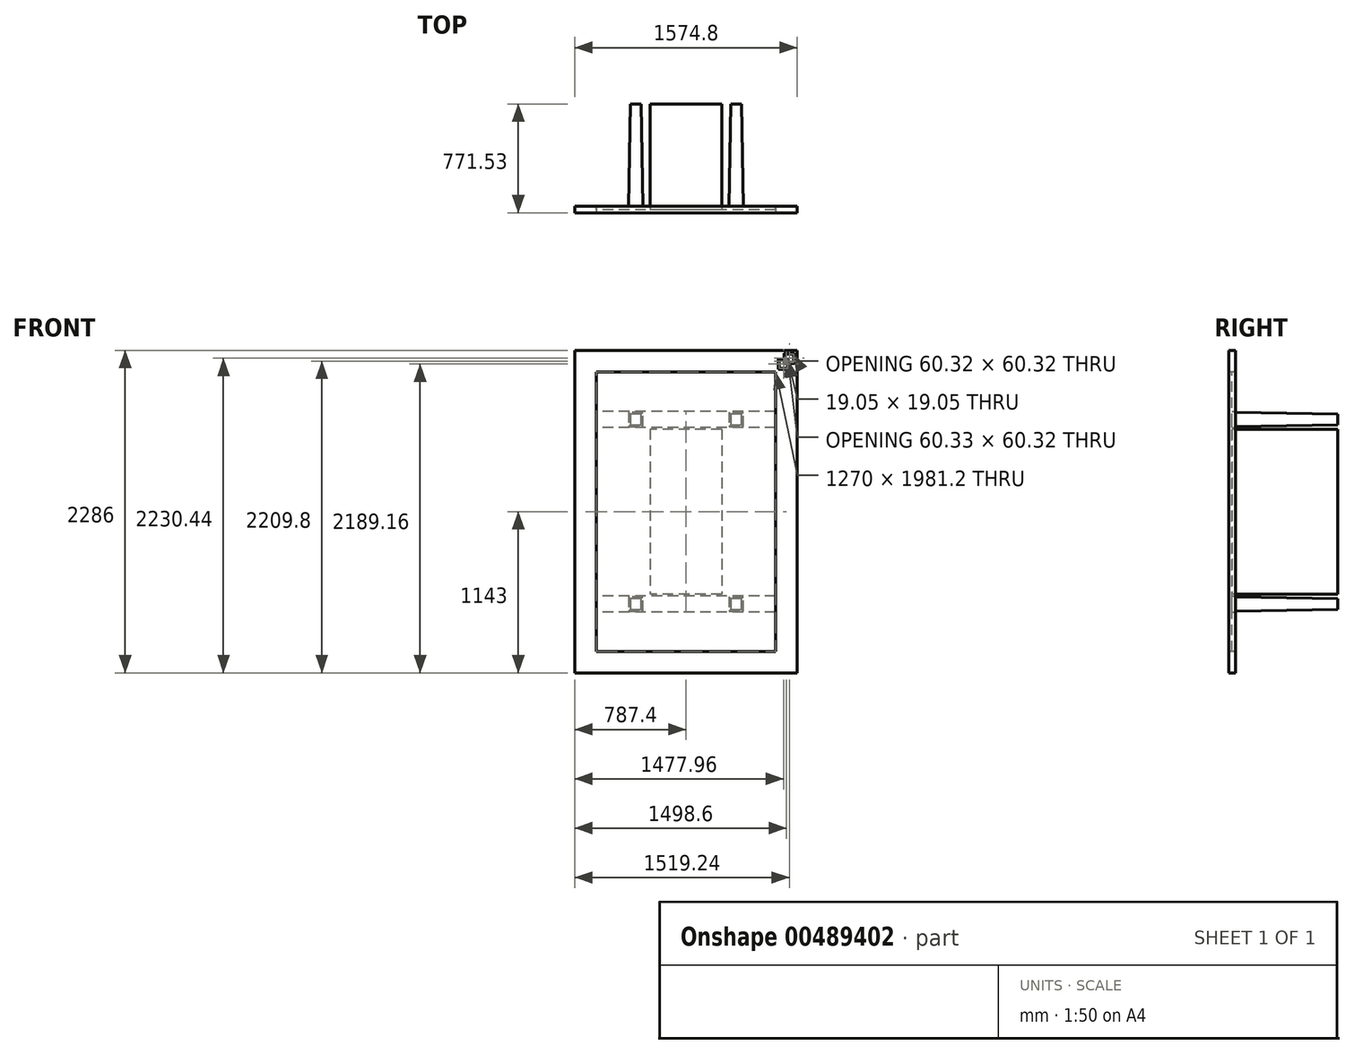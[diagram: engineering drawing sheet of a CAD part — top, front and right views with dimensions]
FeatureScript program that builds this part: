
annotation { "Feature Type Name" : "Feature", "Feature Type Description" : "" }
export const myFeature = defineFeature(function(context is Context, id is Id, definition is map)
    precondition{}
    {
        {
            var Q0;
            Q0=qCreatedBy(makeId("Front.planeOp"),FACE);
            var sketch = newSketch(context, id + "F0", { "sketchPlane" : qUnion([Q0])});
            skLineSegment(sketch, "E0.bottom", {"start": v(0, 0) * mm, "end": v(-1574.8, 0) * mm});
            skLineSegment(sketch, "E0.top", {"start": v(0, 2286) * mm, "end": v(-1574.8, 2286) * mm});
            skLineSegment(sketch, "E0.left", {"start": v(0, 0) * mm, "end": v(0, 2286) * mm});
            skLineSegment(sketch, "E0.right", {"start": v(-1574.8, 0) * mm, "end": v(-1574.8, 2286) * mm});
            skLineSegment(sketch, "E1.0", {"start": v(-152.4, 2133.6) * mm, "end": v(-1422.4, 2133.6) * mm});
            skLineSegment(sketch, "E1.1", {"start": v(-152.4, 152.4) * mm, "end": v(-152.4, 2133.6) * mm});
            skLineSegment(sketch, "E1.2", {"start": v(-152.4, 152.4) * mm, "end": v(-1422.4, 152.4) * mm});
            skLineSegment(sketch, "E1.3", {"start": v(-1422.4, 152.4) * mm, "end": v(-1422.4, 2133.6) * mm});
            skLineSegment(sketch, "E2", {"start": v(-1422.4, 2133.6) * mm, "end": v(-1574.8, 2133.6) * mm});
            skLineSegment(sketch, "E3", {"start": v(-152.4, 2133.6) * mm, "end": v(0, 2133.6) * mm});
            skLineSegment(sketch, "E4", {"start": v(-152.4, 152.4) * mm, "end": v(0, 152.4) * mm});
            skLineSegment(sketch, "E5", {"start": v(-1422.4, 152.4) * mm, "end": v(-1574.8, 152.4) * mm});
            skSolve(sketch);
        }
        {
            var Q0;
            {var subQ1=sQuery(id+"F0.wireOp",EDGE,"E0.top");Q0=makeQuery(id+"F0.imprint","IMPRINT",FACE,{"disambiguationData":[TD([[makeQuery(id+"F0.imprint","IMPRINT",EDGE,{"derivedFrom":subQ1}),1.0]])]});}
            var Q1;
            Q1=makeQuery(id+"F0.imprint","IMPRINT",FACE,{"disambiguationData":[TD([[makeQuery(id+"F0.imprint","IMPRINT",EDGE,{"derivedFrom":sQuery(id+"F0.wireOp",EDGE,"E1.3")}),1.0]])]});
            var Q2;
            Q2=makeQuery(id+"F0.imprint","IMPRINT",FACE,{"disambiguationData":[TD([[makeQuery(id+"F0.imprint","IMPRINT",EDGE,{"derivedFrom":sQuery(id+"F0.wireOp",EDGE,"E1.1")}),-1.0]])]});
            var Q3;
            {var subQ1=sQuery(id+"F0.wireOp",EDGE,"E0.bottom");Q3=makeQuery(id+"F0.imprint","IMPRINT",FACE,{"disambiguationData":[TD([[makeQuery(id+"F0.imprint","IMPRINT",EDGE,{"derivedFrom":subQ1}),-1.0]])]});}
            extrude(context, id + "F1", {"entities" : qUnion([Q0, Q1, Q2, Q3]), "oppositeDirection" : true, "depth" : 47.62 * mm, "offsetDistance" : 25.4 * mm});
        }
        {
            var Q0;
            Q0=makeQuery(id+"F0.imprint","IMPRINT",FACE,{"disambiguationData":[TD([[makeQuery(id+"F0.imprint","IMPRINT",EDGE,{"derivedFrom":sQuery(id+"F0.wireOp",EDGE,"E1.0")}),1.0]])]});
            extrude(context, id + "F2", {"entities" : qUnion([Q0]), "oppositeDirection" : true, "depth" : 22.22 * mm, "offsetDistance" : 25.4 * mm});
        }
        {
            var Q0;
            Q0=makeQuery(id+"F1.opExtrude","SWEPT_FACE",FACE,{"disambiguationData":[OSD([sQuery(id+"F0.wireOp",EDGE,"E1.3")])]});
            var sketch = newSketch(context, id + "F3", { "sketchPlane" : qUnion([Q0])});
            skLineSegment(sketch, "E6.bottom", {"start": v(22.23, 431.8) * mm, "end": v(47.62, 431.8) * mm});
            skLineSegment(sketch, "E6.top", {"start": v(22.22, 546.1) * mm, "end": v(47.63, 546.1) * mm});
            skLineSegment(sketch, "E6.left", {"start": v(22.23, 431.8) * mm, "end": v(22.22, 546.1) * mm});
            skLineSegment(sketch, "E6.right", {"start": v(47.63, 431.8) * mm, "end": v(47.63, 546.1) * mm});
            skLineSegment(sketch, "E7.bottom", {"start": v(22.23, 1739.9) * mm, "end": v(47.63, 1739.9) * mm});
            skLineSegment(sketch, "E7.top", {"start": v(22.23, 1854.2) * mm, "end": v(47.63, 1854.2) * mm});
            skLineSegment(sketch, "E7.left", {"start": v(22.23, 1739.9) * mm, "end": v(22.23, 1854.2) * mm});
            skLineSegment(sketch, "E7.right", {"start": v(47.63, 1739.9) * mm, "end": v(47.63, 1854.2) * mm});
            skSolve(sketch);
        }
        {
            var Q0;
            Q0=makeQuery(id+"F3.imprint","IMPRINT",FACE,{"disambiguationData":[TD([[makeQuery(id+"F3.imprint","IMPRINT",EDGE,{"derivedFrom":sQuery(id+"F3.wireOp",EDGE,"E6.bottom")}),1.0]])]});
            var Q1;
            Q1=makeQuery(id+"F3.imprint","IMPRINT",FACE,{"disambiguationData":[TD([[makeQuery(id+"F3.imprint","IMPRINT",EDGE,{"derivedFrom":sQuery(id+"F3.wireOp",EDGE,"E7.bottom")}),1.0]])]});
            var Q2;
            Q2=makeQuery(id+"F1.opExtrude","SWEPT_FACE",FACE,{"disambiguationData":[OSD([sQuery(id+"F0.wireOp",EDGE,"E1.1")])]});
            extrude(context, id + "F4", {"entities" : qUnion([Q0, Q1]), "endBound" : BoundingType.UP_TO_SURFACE, "depth" : 25.4 * mm, "endBoundEntityFace" : qUnion([Q2]), "offsetDistance" : 25.4 * mm});
        }
        {
            var Q0;
            Q0=makeQuery(id+"F1.opExtrude","CAP_FACE",FACE,{"disambiguationData":[OSD([sQuery(id+"F0.wireOp",EDGE,"E0.bottom"),sQuery(id+"F0.wireOp",EDGE,"E0.top"),sQuery(id+"F0.wireOp",EDGE,"E0.left"),sQuery(id+"F0.wireOp",EDGE,"E0.right"),sQuery(id+"F0.wireOp",EDGE,"E1.0"),sQuery(id+"F0.wireOp",EDGE,"E1.1"),sQuery(id+"F0.wireOp",EDGE,"E1.2"),sQuery(id+"F0.wireOp",EDGE,"E1.3")])],"isStart":false});
            var sketch = newSketch(context, id + "F5", { "sketchPlane" : qUnion([Q0])});
            skLineSegment(sketch, "E8.bottom", {"start": v(381, 1847.53) * mm, "end": v(482.6, 1847.53) * mm});
            skLineSegment(sketch, "E8.top", {"start": v(381, 1745.93) * mm, "end": v(482.6, 1745.93) * mm});
            skLineSegment(sketch, "E8.left", {"start": v(381, 1847.53) * mm, "end": v(381, 1745.93) * mm});
            skLineSegment(sketch, "E8.right", {"start": v(482.6, 1847.53) * mm, "end": v(482.6, 1745.93) * mm});
            skLineSegment(sketch, "E9.0.1.0", {"start": v(482.6, 539.43) * mm, "end": v(482.6, 437.83) * mm});
            skLineSegment(sketch, "E9.0.1.1", {"start": v(381, 539.43) * mm, "end": v(381, 437.83) * mm});
            skLineSegment(sketch, "E9.0.1.2", {"start": v(381, 437.83) * mm, "end": v(482.6, 437.83) * mm});
            skLineSegment(sketch, "E9.0.1.3", {"start": v(381, 539.43) * mm, "end": v(482.6, 539.43) * mm});
            skLineSegment(sketch, "E9.1.0.0", {"start": v(1193.8, 1847.53) * mm, "end": v(1193.8, 1745.93) * mm});
            skLineSegment(sketch, "E9.1.0.1", {"start": v(1092.2, 1847.53) * mm, "end": v(1092.2, 1745.93) * mm});
            skLineSegment(sketch, "E9.1.0.2", {"start": v(1092.2, 1745.93) * mm, "end": v(1193.8, 1745.93) * mm});
            skLineSegment(sketch, "E9.1.0.3", {"start": v(1092.2, 1847.53) * mm, "end": v(1193.8, 1847.53) * mm});
            skLineSegment(sketch, "E9.1.1.0", {"start": v(1193.8, 539.43) * mm, "end": v(1193.8, 437.83) * mm});
            skLineSegment(sketch, "E9.1.1.1", {"start": v(1092.2, 539.43) * mm, "end": v(1092.2, 437.83) * mm});
            skLineSegment(sketch, "E9.1.1.2", {"start": v(1092.2, 437.83) * mm, "end": v(1193.8, 437.83) * mm});
            skLineSegment(sketch, "E9.1.1.3", {"start": v(1092.2, 539.43) * mm, "end": v(1193.8, 539.43) * mm});
            skLineSegment(sketch, "E9.direction1", {"start": v(381, 1745.93) * mm, "end": v(1092.2, 1745.93) * mm, "construction": true});
            skLineSegment(sketch, "E9.direction2", {"start": v(381, 1745.93) * mm, "end": v(381, 437.83) * mm, "construction": true});
            skSolve(sketch);
        }
        {
            var Q0;
            Q0=makeQuery(id+"F5.imprint","IMPRINT",FACE,{"disambiguationData":[TD([[makeQuery(id+"F5.imprint","IMPRINT",EDGE,{"derivedFrom":sQuery(id+"F5.wireOp",EDGE,"E8.bottom")}),-1.0]])]});
            var Q1;
            Q1=makeQuery(id+"F5.imprint","IMPRINT",FACE,{"disambiguationData":[TD([[makeQuery(id+"F5.imprint","IMPRINT",EDGE,{"derivedFrom":sQuery(id+"F5.wireOp",EDGE,"E9.1.0.0")}),-1.0]])]});
            var Q2;
            Q2=makeQuery(id+"F5.imprint","IMPRINT",FACE,{"disambiguationData":[TD([[makeQuery(id+"F5.imprint","IMPRINT",EDGE,{"derivedFrom":sQuery(id+"F5.wireOp",EDGE,"E9.0.1.0")}),-1.0]])]});
            var Q3;
            Q3=makeQuery(id+"F5.imprint","IMPRINT",FACE,{"disambiguationData":[TD([[makeQuery(id+"F5.imprint","IMPRINT",EDGE,{"derivedFrom":sQuery(id+"F5.wireOp",EDGE,"E9.1.1.0")}),-1.0]])]});
            extrude(context, id + "F6", {"entities" : qUnion([Q0, Q1, Q2, Q3]), "depth" : 723.9 * mm, "offsetDistance" : 25.4 * mm, "hasDraft" : true, "draftAngle" : 1 * degree, "draftPullDirection" : true});
        }
        {
            var Q0;
            Q0=makeQuery(id+"F2.opExtrude","CAP_FACE",FACE,{"disambiguationData":[OSD([sQuery(id+"F0.wireOp",EDGE,"E1.0"),sQuery(id+"F0.wireOp",EDGE,"E1.1"),sQuery(id+"F0.wireOp",EDGE,"E1.2"),sQuery(id+"F0.wireOp",EDGE,"E1.3")])],"isStart":false});
            var sketch = newSketch(context, id + "F7", { "sketchPlane" : qUnion([Q0])});
            skLineSegment(sketch, "E10.bottom", {"start": v(533.4, 1727.2) * mm, "end": v(1041.4, 1727.2) * mm});
            skLineSegment(sketch, "E10.top", {"start": v(533.4, 558.8) * mm, "end": v(1041.4, 558.8) * mm});
            skLineSegment(sketch, "E10.left", {"start": v(533.4, 1727.2) * mm, "end": v(533.4, 558.8) * mm});
            skLineSegment(sketch, "E10.right", {"start": v(1041.4, 1727.2) * mm, "end": v(1041.4, 558.8) * mm});
            skPoint(sketch, "E10.middle", {"position": v(787.4, 1143) * mm});
            skPoint(sketch, "E10.middle.positionSnap0", {"position": v(152.4, 1143) * mm});
            skPoint(sketch, "E10.middle.positionSnap1", {"position": v(787.4, 152.4) * mm});
            skPoint(sketch, "E10.centerSnap0", {"position": v(152.4, 1143) * mm});
            skPoint(sketch, "E10.centerSnap1", {"position": v(787.4, 152.4) * mm});
            skSolve(sketch);
        }
        {
            var Q0;
            Q0 = qSketchRegion(id + "F7", true);
            var Q1;
            Q1=makeQuery(id+"F6.opExtrude","CAP_FACE",FACE,{"disambiguationData":[OSD([sQuery(id+"F5.wireOp",EDGE,"E8.bottom"),sQuery(id+"F5.wireOp",EDGE,"E8.top"),sQuery(id+"F5.wireOp",EDGE,"E8.left"),sQuery(id+"F5.wireOp",EDGE,"E8.right")])],"isStart":false});
            extrude(context, id + "F8", {"entities" : qUnion([Q0]), "endBound" : BoundingType.UP_TO_SURFACE, "depth" : 533.4 * mm, "endBoundEntityFace" : qUnion([Q1]), "offsetDistance" : 25.4 * mm});
        }
        {
            var Q0;
            Q0=makeQuery(id+"F1.opExtrude","CAP_FACE",FACE,{"disambiguationData":[OSD([sQuery(id+"F0.wireOp",EDGE,"E0.bottom"),sQuery(id+"F0.wireOp",EDGE,"E0.top"),sQuery(id+"F0.wireOp",EDGE,"E0.left"),sQuery(id+"F0.wireOp",EDGE,"E0.right"),sQuery(id+"F0.wireOp",EDGE,"E1.0"),sQuery(id+"F0.wireOp",EDGE,"E1.1"),sQuery(id+"F0.wireOp",EDGE,"E1.2"),sQuery(id+"F0.wireOp",EDGE,"E1.3")])],"isStart":true});
            var sketch = newSketch(context, id + "F9", { "sketchPlane" : qUnion([Q0])});
            skLineSegment(sketch, "E11.bottom", {"start": v(-92.07, 2193.92) * mm, "end": v(-19.05, 2193.92) * mm});
            skLineSegment(sketch, "E11.top", {"start": v(-92.07, 2266.95) * mm, "end": v(-19.05, 2266.95) * mm});
            skLineSegment(sketch, "E11.left", {"start": v(-92.07, 2193.92) * mm, "end": v(-92.07, 2266.95) * mm});
            skLineSegment(sketch, "E11.right", {"start": v(-19.05, 2193.92) * mm, "end": v(-19.05, 2266.95) * mm});
            skPoint(sketch, "E11.middle", {"position": v(-55.56, 2230.44) * mm});
            skLineSegment(sketch, "E12.bottom", {"start": v(-133.35, 2152.65) * mm, "end": v(-60.32, 2152.65) * mm});
            skLineSegment(sketch, "E12.top", {"start": v(-133.35, 2225.67) * mm, "end": v(-60.32, 2225.67) * mm});
            skLineSegment(sketch, "E12.left", {"start": v(-133.35, 2152.65) * mm, "end": v(-133.35, 2225.67) * mm});
            skLineSegment(sketch, "E12.right", {"start": v(-60.32, 2152.65) * mm, "end": v(-60.32, 2225.67) * mm});
            skPoint(sketch, "E12.middle", {"position": v(-96.84, 2189.16) * mm});
            skLineSegment(sketch, "E13.0", {"start": v(-25.4, 2200.28) * mm, "end": v(-25.4, 2260.6) * mm});
            skLineSegment(sketch, "E13.1", {"start": v(-85.72, 2200.28) * mm, "end": v(-25.4, 2200.28) * mm});
            skLineSegment(sketch, "E13.2", {"start": v(-85.72, 2200.28) * mm, "end": v(-85.72, 2260.6) * mm});
            skLineSegment(sketch, "E13.3", {"start": v(-85.72, 2260.6) * mm, "end": v(-25.4, 2260.6) * mm});
            skLineSegment(sketch, "E14.0", {"start": v(-127, 2219.32) * mm, "end": v(-66.67, 2219.32) * mm});
            skLineSegment(sketch, "E14.1", {"start": v(-127, 2159) * mm, "end": v(-127, 2219.32) * mm});
            skLineSegment(sketch, "E14.2", {"start": v(-127, 2159) * mm, "end": v(-66.67, 2159) * mm});
            skLineSegment(sketch, "E14.3", {"start": v(-66.67, 2159) * mm, "end": v(-66.67, 2219.32) * mm});
            skLineSegment(sketch, "E15", {"start": v(0, 2286) * mm, "end": v(-152.4, 2133.6) * mm, "construction": true});
            skSolve(sketch);
        }
        {
            var Q0;
            {var subQ1=sQuery(id+"F9.wireOp",EDGE,"E11.top");Q0=makeQuery(id+"F9.imprint","IMPRINT",FACE,{"disambiguationData":[TD([[makeQuery(id+"F9.imprint","IMPRINT",EDGE,{"derivedFrom":subQ1}),-1.0]])]});}
            var Q1;
            {var subQ0=sQuery(id+"F9.wireOp",EDGE,"E11.left");var subQ1=sQuery(id+"F9.wireOp",EDGE,"E11.bottom");var subQ2=makeQuery(id+"F9.imprint","INTERSECT",VERTEX,{"derivedFrom":[subQ1,subQ0]});Q1=makeQuery(id+"F9.imprint","IMPRINT",FACE,{"disambiguationData":[TD([[makeQuery(id+"F9.imprint","IMPRINT",EDGE,{"disambiguationData":[TD([[subQ2,-1.0]])],"derivedFrom":subQ1}),1.0]])]});}
            var Q2;
            {var subQ0=sQuery(id+"F9.wireOp",EDGE,"E14.3");var subQ1=sQuery(id+"F9.wireOp",EDGE,"E11.bottom");var subQ2=makeQuery(id+"F9.imprint","INTERSECT",VERTEX,{"derivedFrom":[subQ1,subQ0]});Q2=makeQuery(id+"F9.imprint","IMPRINT",FACE,{"disambiguationData":[TD([[makeQuery(id+"F9.imprint","IMPRINT",EDGE,{"disambiguationData":[TD([[subQ2,-1.0]])],"derivedFrom":subQ1}),1.0]])]});}
            var Q3;
            {var subQ1=sQuery(id+"F9.wireOp",EDGE,"E12.right");var subQ5=sQuery(id+"F9.wireOp",EDGE,"E12.top");var subQ6=makeQuery(id+"F9.imprint","INTERSECT",VERTEX,{"derivedFrom":[subQ5,subQ1]});Q3=makeQuery(id+"F9.imprint","IMPRINT",FACE,{"disambiguationData":[TD([[makeQuery(id+"F9.imprint","IMPRINT",EDGE,{"disambiguationData":[TD([[subQ6,1.0]])],"derivedFrom":subQ5}),-1.0]])]});}
            var Q4;
            {var subQ0=sQuery(id+"F9.wireOp",EDGE,"E14.0");var subQ1=sQuery(id+"F9.wireOp",EDGE,"E11.left");var subQ2=makeQuery(id+"F9.imprint","INTERSECT",VERTEX,{"derivedFrom":[subQ1,subQ0]});Q4=makeQuery(id+"F9.imprint","IMPRINT",FACE,{"disambiguationData":[TD([[makeQuery(id+"F9.imprint","IMPRINT",EDGE,{"disambiguationData":[TD([[subQ2,-1.0]])],"derivedFrom":subQ1}),-1.0]])]});}
            var Q5;
            {var subQ4=sQuery(id+"F9.wireOp",EDGE,"E12.bottom");Q5=makeQuery(id+"F9.imprint","IMPRINT",FACE,{"disambiguationData":[TD([[makeQuery(id+"F9.imprint","IMPRINT",EDGE,{"derivedFrom":subQ4}),1.0]])]});}
            extrude(context, id + "F10", {"entities" : qUnion([Q0, Q1, Q2, Q3, Q4, Q5]), "operationType" : NewBodyOperationType.REMOVE, "oppositeDirection" : true, "depth" : 0.4 * mm, "offsetDistance" : 25.4 * mm});
        }
        {
            var Q0;
            Q0=makeQuery(id+"F10.boolean.opBoolean","COPY",FACE,{"derivedFrom":makeQuery(id+"F10.opExtrude","CAP_FACE",FACE,{"disambiguationData":[OSD([sQuery(id+"F9.wireOp",EDGE,"E11.bottom"),sQuery(id+"F9.wireOp",EDGE,"E11.top"),sQuery(id+"F9.wireOp",EDGE,"E11.left"),sQuery(id+"F9.wireOp",EDGE,"E11.right"),sQuery(id+"F9.wireOp",EDGE,"E12.bottom"),sQuery(id+"F9.wireOp",EDGE,"E12.top"),sQuery(id+"F9.wireOp",EDGE,"E12.left"),sQuery(id+"F9.wireOp",EDGE,"E12.right"),sQuery(id+"F9.wireOp",EDGE,"E13.0"),sQuery(id+"F9.wireOp",EDGE,"E13.1"),sQuery(id+"F9.wireOp",EDGE,"E13.2"),sQuery(id+"F9.wireOp",EDGE,"E13.3"),sQuery(id+"F9.wireOp",EDGE,"E14.0"),sQuery(id+"F9.wireOp",EDGE,"E14.1"),sQuery(id+"F9.wireOp",EDGE,"E14.2"),sQuery(id+"F9.wireOp",EDGE,"E14.3")])],"isStart":false})});
            var Q1;
            {var subQ0=sQuery(id+"F0.wireOp",EDGE,"E1.3");var subQ1=sQuery(id+"F0.wireOp",EDGE,"E1.2");var subQ2=sQuery(id+"F0.wireOp",EDGE,"E1.1");var subQ7=sQuery(id+"F0.wireOp",EDGE,"E1.0");var subQ9=sQuery(id+"F0.wireOp",EDGE,"E0.bottom");var subQ11=sQuery(id+"F0.wireOp",EDGE,"E0.right");var subQ12=sQuery(id+"F0.wireOp",EDGE,"E0.top");var subQ14=sQuery(id+"F0.wireOp",EDGE,"E0.left");Q1=makeQuery(id+"F10.boolean.opBoolean","SPLIT",FACE,{"disambiguationData":[TD([makeQuery(id+"F1.opExtrude","SWEPT_FACE",FACE,{"disambiguationData":[OSD([subQ9])]})])],"derivedFrom":makeQuery(id+"F1.opExtrude","CAP_FACE",FACE,{"disambiguationData":[OSD([subQ9,subQ12,subQ14,subQ11,subQ7,subQ2,subQ1,subQ0])],"isStart":true})});}
            extrude(context, id + "F11", {"entities" : qUnion([Q0]), "endBound" : BoundingType.UP_TO_SURFACE, "depth" : 25.4 * mm, "endBoundEntityFace" : qUnion([Q1]), "offsetDistance" : 25.4 * mm});
        }
    });
